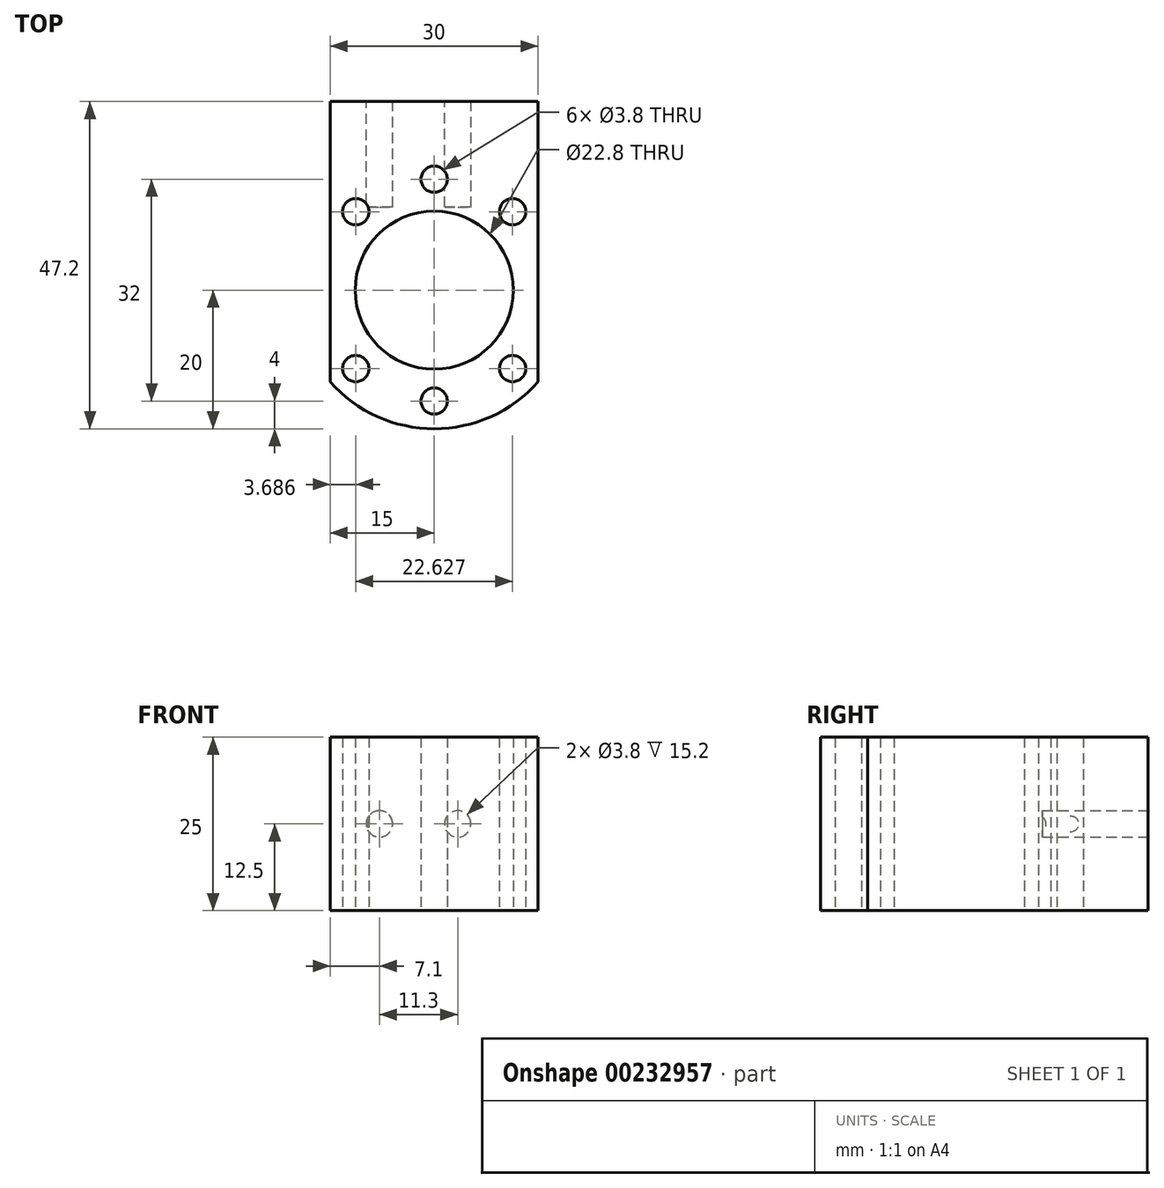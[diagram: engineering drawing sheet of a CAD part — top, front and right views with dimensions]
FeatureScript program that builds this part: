
annotation { "Feature Type Name" : "Feature", "Feature Type Description" : "" }
export const myFeature = defineFeature(function(context is Context, id is Id, definition is map)
    precondition{}
    {
        {
            var Q0;
            Q0=qCreatedBy(makeId("Top.planeOp"),FACE);
            var sketch = newSketch(context, id + "F0", { "sketchPlane" : qUnion([Q0])});
            skLineSegment(sketch, "E0.bottom", {"start": v(15, -27.2) * mm, "end": v(-15, -27.2) * mm});
            skLineSegment(sketch, "E0.top", {"start": v(15, 27.2) * mm, "end": v(-15, 27.2) * mm});
            skLineSegment(sketch, "E0.left", {"start": v(15, -27.2) * mm, "end": v(15, 27.2) * mm});
            skLineSegment(sketch, "E0.right", {"start": v(-15, -27.2) * mm, "end": v(-15, 27.2) * mm});
            skPoint(sketch, "E0.middle", {"position": v(0, 0) * mm});
            skCircle(sketch, "E1", {"center": v(0, 0) * mm, "radius": 11.4 * mm});
            skCircle(sketch, "E2", {"center": v(0, 0) * mm, "radius": 20 * mm});
            skCircle(sketch, "E3", {"center": v(0, 0) * mm, "radius": 16 * mm, "construction": true});
            skLineSegment(sketch, "E4", {"start": v(0, 24.12) * mm, "end": v(0, -31.78) * mm, "construction": true});
            skCircle(sketch, "E5", {"center": v(0, 16) * mm, "radius": 1.9 * mm});
            skCircle(sketch, "E6", {"center": v(0, -16) * mm, "radius": 1.9 * mm});
            skLineSegment(sketch, "E7", {"start": v(23.54, 23.54) * mm, "end": v(-27.74, -27.74) * mm, "construction": true});
            skLineSegment(sketch, "E8", {"start": v(22.85, -22.85) * mm, "end": v(-18.77, 18.77) * mm, "construction": true});
            skCircle(sketch, "E9", {"center": v(11.31, 11.31) * mm, "radius": 1.9 * mm});
            skCircle(sketch, "E10", {"center": v(-11.31, 11.31) * mm, "radius": 1.9 * mm});
            skCircle(sketch, "E11", {"center": v(-11.31, -11.31) * mm, "radius": 1.9 * mm});
            skCircle(sketch, "E12", {"center": v(11.31, -11.31) * mm, "radius": 1.9 * mm});
            skSolve(sketch);
        }
        {
            var Q0;
            {var subQ0=sQuery(id+"F0.wireOp",EDGE,"E0.left");var subQ1=sQuery(id+"F0.wireOp",EDGE,"E0.top");var subQ2=makeQuery(id+"F0.imprint","INTERSECT",VERTEX,{"derivedFrom":[subQ1,subQ0]});Q0=makeQuery(id+"F0.imprint","IMPRINT",FACE,{"disambiguationData":[TD([[makeQuery(id+"F0.imprint","IMPRINT",EDGE,{"disambiguationData":[TD([[subQ2,-1.0]])],"derivedFrom":subQ1}),1.0]])]});}
            var Q1;
            Q1=makeQuery(id+"F0.imprint","IMPRINT",FACE,{"disambiguationData":[TD([[makeQuery(id+"F0.imprint","IMPRINT",EDGE,{"derivedFrom":sQuery(id+"F0.wireOp",EDGE,"E1")}),-1.0]])]});
            var Q2;
            {var subQ0=sQuery(id+"F0.wireOp",EDGE,"E0.right");var subQ1=sQuery(id+"F0.wireOp",EDGE,"E0.top");var subQ2=makeQuery(id+"F0.imprint","INTERSECT",VERTEX,{"derivedFrom":[subQ1,subQ0]});Q2=makeQuery(id+"F0.imprint","IMPRINT",FACE,{"disambiguationData":[TD([[makeQuery(id+"F0.imprint","IMPRINT",EDGE,{"disambiguationData":[TD([[subQ2,1.0]])],"derivedFrom":subQ1}),1.0]])]});}
            extrude(context, id + "F1", {"entities" : qUnion([Q0, Q1, Q2]), "depth" : 25 * mm});
        }
        {
            var Q0;
            Q0=makeQuery(id+"F1.opExtrude","SWEPT_FACE",FACE,{"disambiguationData":[OSD([sQuery(id+"F0.wireOp",EDGE,"E0.top")])]});
            var sketch = newSketch(context, id + "F2", { "sketchPlane" : qUnion([Q0])});
            skLineSegment(sketch, "E13", {"start": v(-15, 12.5) * mm, "end": v(15, 12.5) * mm});
            skPoint(sketch, "E14", {"position": v(0, 12.5) * mm});
            skCircle(sketch, "E15", {"center": v(-3.4, 12.5) * mm, "radius": 1.9 * mm});
            skCircle(sketch, "E16", {"center": v(7.9, 12.5) * mm, "radius": 1.9 * mm});
            skSolve(sketch);
        }
        {
            var Q0;
            Q0 = qSketchRegion(id + "F2", true);
            extrude(context, id + "F3", {"entities" : qUnion([Q0]), "operationType" : NewBodyOperationType.REMOVE, "oppositeDirection" : true, "depth" : 15.2 * mm});
        }
    });
